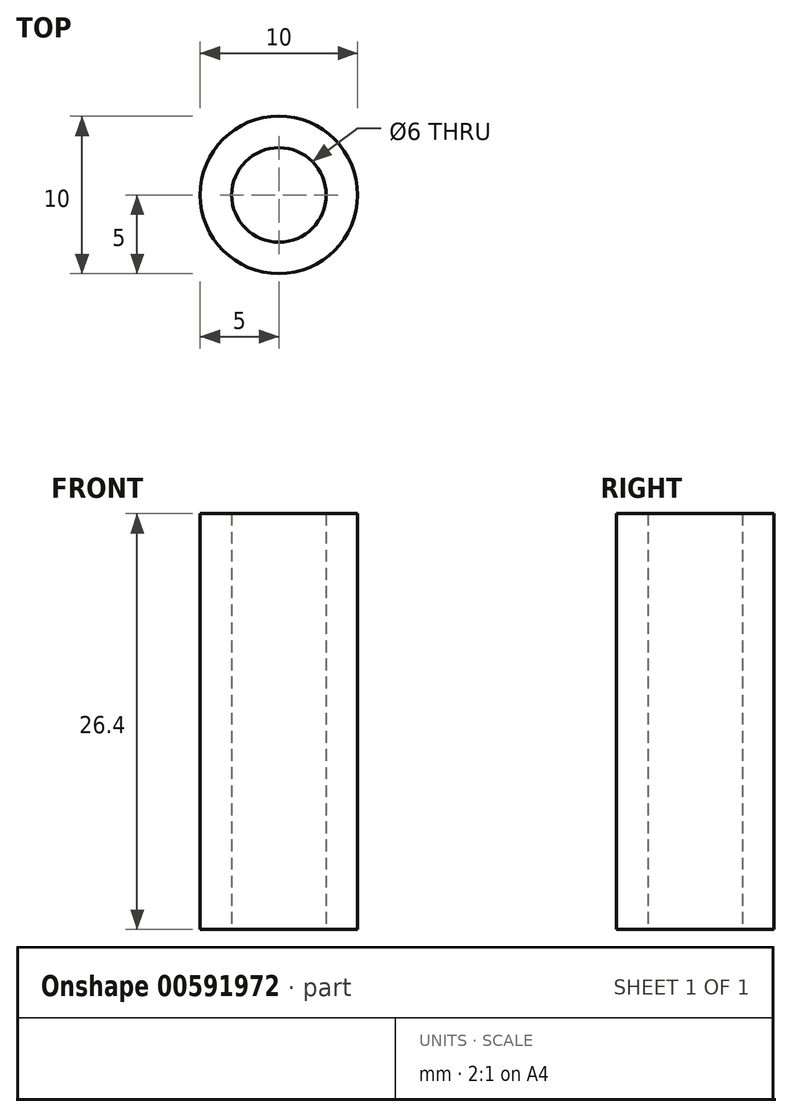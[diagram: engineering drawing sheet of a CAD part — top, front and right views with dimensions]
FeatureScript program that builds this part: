
annotation { "Feature Type Name" : "Feature", "Feature Type Description" : "" }
export const myFeature = defineFeature(function(context is Context, id is Id, definition is map)
    precondition{}
    {
        {
            var Q0;
            Q0=qCreatedBy(makeId("Top.planeOp"),FACE);
            var sketch = newSketch(context, id + "F0", { "sketchPlane" : qUnion([Q0])});
            skCircle(sketch, "E0", {"center": v(0, 0) * mm, "radius": 5 * mm});
            skCircle(sketch, "E1", {"center": v(0, 0) * mm, "radius": 3 * mm});
            skSolve(sketch);
        }
        {
            var Q0;
            Q0=makeQuery(id+"F0.imprint","IMPRINT",FACE,{"disambiguationData":[TD([[makeQuery(id+"F0.imprint","IMPRINT",EDGE,{"derivedFrom":sQuery(id+"F0.wireOp",EDGE,"E0")}),1.0]])]});
            extrude(context, id + "F1", {"entities" : qUnion([Q0]), "depth" : 26.4 * mm, "offsetDistance" : 25.4 * mm});
        }
    });
